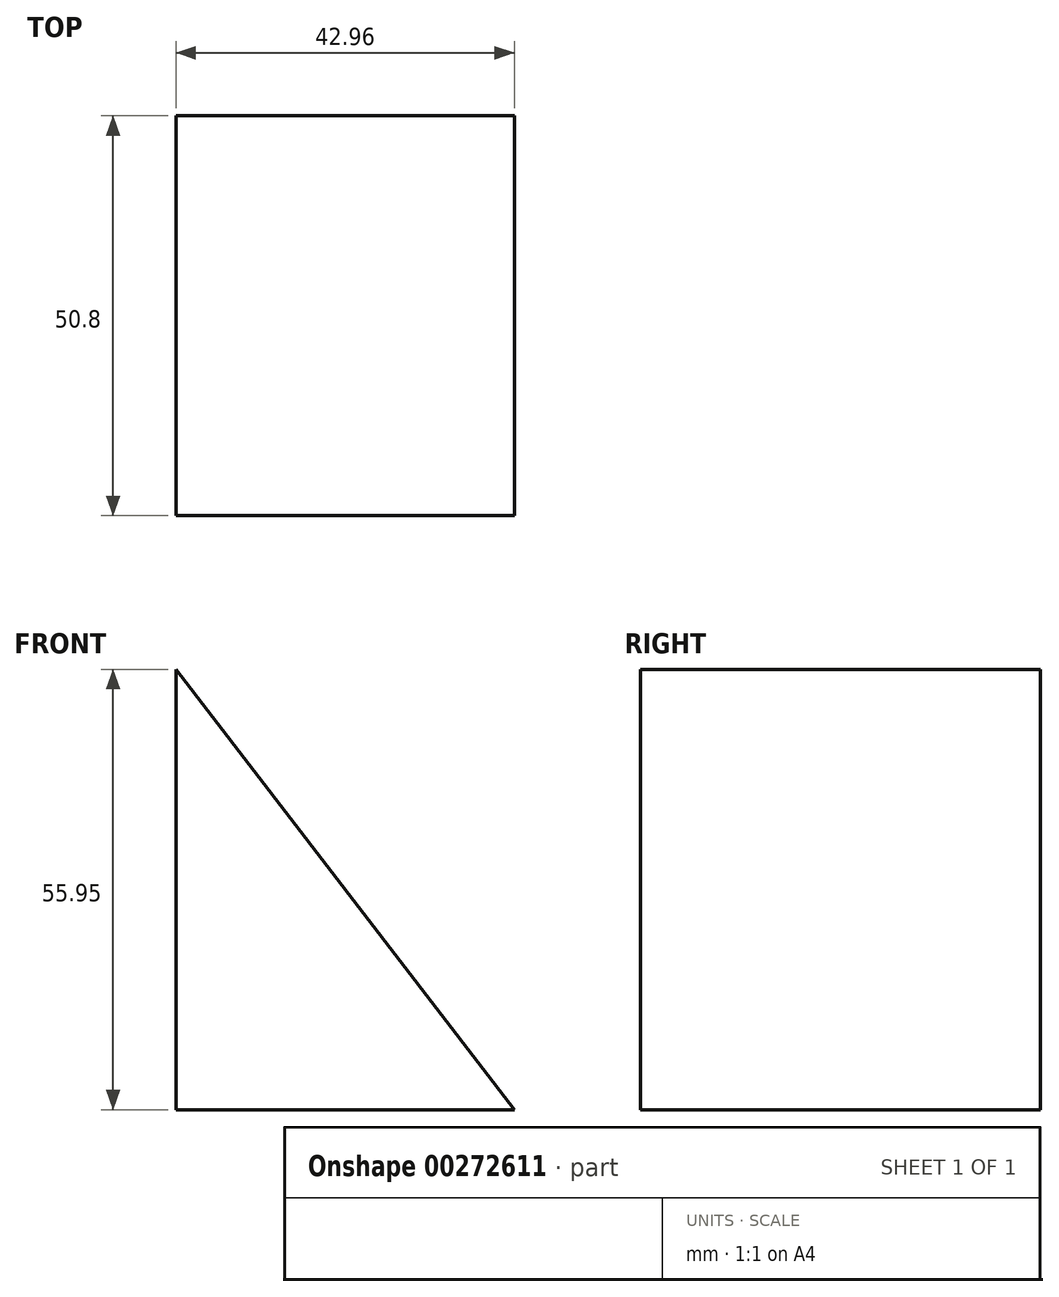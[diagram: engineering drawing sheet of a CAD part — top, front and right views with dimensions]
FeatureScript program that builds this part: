
annotation { "Feature Type Name" : "Feature", "Feature Type Description" : "" }
export const myFeature = defineFeature(function(context is Context, id is Id, definition is map)
    precondition{}
    {
        {
            var Q0;
            Q0=qCreatedBy(makeId("Front.planeOp"),FACE);
            var sketch = newSketch(context, id + "F0", { "sketchPlane" : qUnion([Q0])});
            skLineSegment(sketch, "E0", {"start": v(-42.96, 55.95) * mm, "end": v(-42.96, 0) * mm});
            skLineSegment(sketch, "E1", {"start": v(-42.96, 0) * mm, "end": v(0, 0) * mm});
            skLineSegment(sketch, "E2", {"start": v(0, 0) * mm, "end": v(-42.96, 55.95) * mm});
            skSolve(sketch);
        }
        {
            var Q0;
            Q0 = qSketchRegion(id + "F0", true);
            extrude(context, id + "F1", {"entities" : qUnion([Q0]), "depth" : 50.8 * mm});
        }
    });
